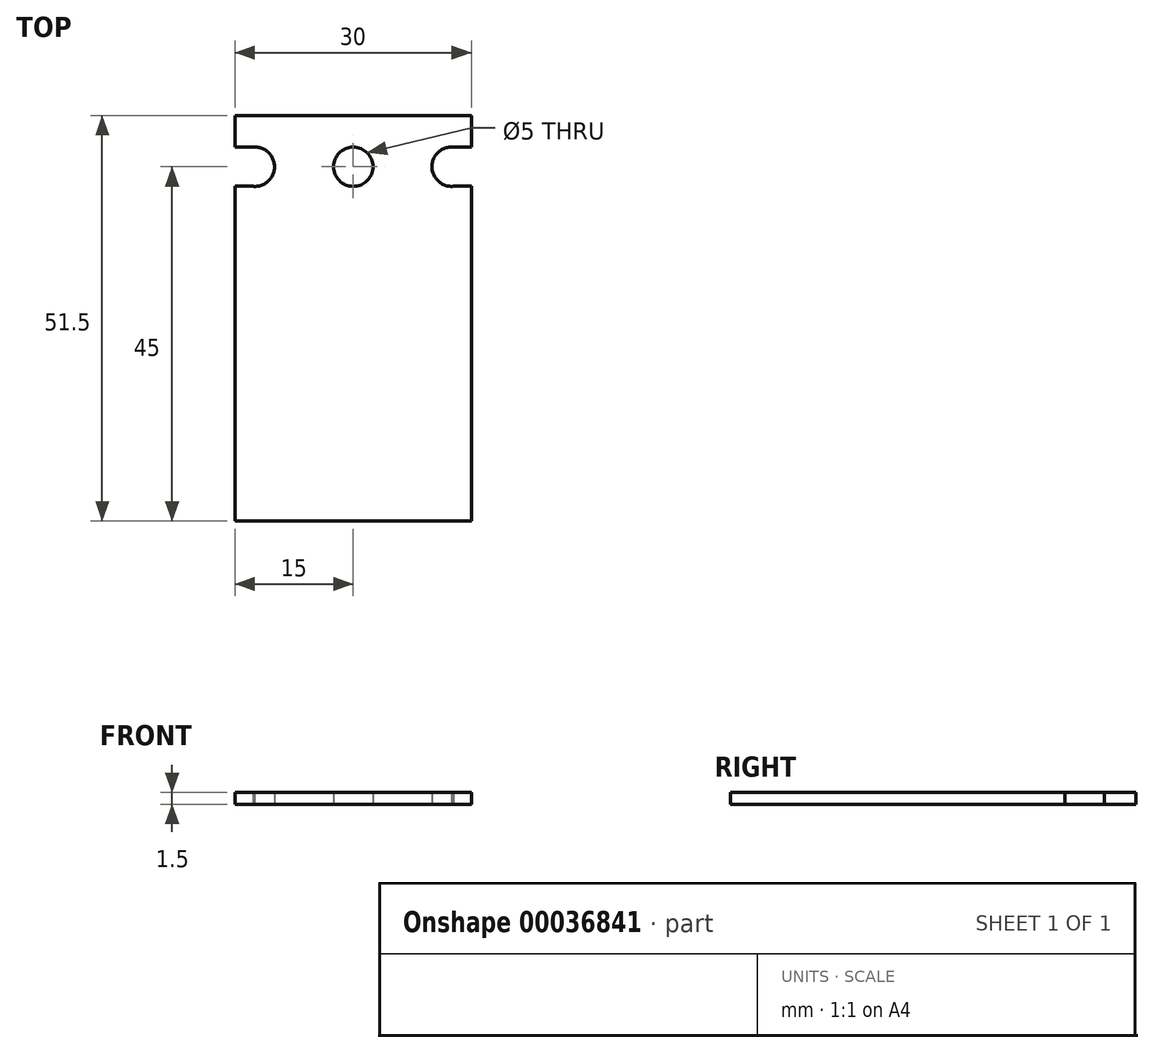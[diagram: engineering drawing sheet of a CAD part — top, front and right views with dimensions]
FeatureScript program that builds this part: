
annotation { "Feature Type Name" : "Feature", "Feature Type Description" : "" }
export const myFeature = defineFeature(function(context is Context, id is Id, definition is map)
    precondition{}
    {
        {
            var Q0;
            Q0=qCreatedBy(makeId("Top.planeOp"),FACE);
            var sketch = newSketch(context, id + "F0", { "sketchPlane" : qUnion([Q0])});
            skLineSegment(sketch, "E0.bottom", {"start": v(-15, 51.5) * mm, "end": v(15, 51.5) * mm});
            skLineSegment(sketch, "E0.top", {"start": v(-15, 0) * mm, "end": v(15, 0) * mm});
            skLineSegment(sketch, "E0.left", {"start": v(-15, 51.5) * mm, "end": v(-15, 0) * mm});
            skLineSegment(sketch, "E0.right", {"start": v(15, 51.5) * mm, "end": v(15, 0) * mm});
            skSolve(sketch);
        }
        {
            var Q0;
            Q0=qCreatedBy(makeId("Top.planeOp"),FACE);
            var sketch = newSketch(context, id + "F1", { "sketchPlane" : qUnion([Q0])});
            skCircle(sketch, "E1", {"center": v(0, 45) * mm, "radius": 2.5 * mm});
            skCircle(sketch, "E2", {"center": v(-12.5, 45) * mm, "radius": 2.5 * mm});
            skCircle(sketch, "E3", {"center": v(12.5, 45) * mm, "radius": 2.5 * mm});
            skLineSegment(sketch, "E4.bottom", {"start": v(12.5, 47.51) * mm, "end": v(15.09, 47.51) * mm});
            skLineSegment(sketch, "E4.top", {"start": v(12.5, 42.51) * mm, "end": v(15.09, 42.51) * mm});
            skLineSegment(sketch, "E4.left", {"start": v(12.5, 47.51) * mm, "end": v(12.5, 42.51) * mm});
            skLineSegment(sketch, "E4.right", {"start": v(15.09, 47.51) * mm, "end": v(15.09, 42.51) * mm});
            skLineSegment(sketch, "E5.bottom", {"start": v(-12.51, 47.51) * mm, "end": v(-15.01, 47.51) * mm});
            skLineSegment(sketch, "E5.top", {"start": v(-12.51, 42.51) * mm, "end": v(-15.01, 42.51) * mm});
            skLineSegment(sketch, "E5.left", {"start": v(-12.51, 47.51) * mm, "end": v(-12.51, 42.51) * mm});
            skLineSegment(sketch, "E5.right", {"start": v(-15.01, 47.51) * mm, "end": v(-15.01, 42.51) * mm});
            skSolve(sketch);
        }
        {
            var Q0;
            Q0=makeQuery(id+"F0.imprint","IMPRINT",FACE,{"disambiguationData":[TD([[makeQuery(id+"F0.imprint","IMPRINT",EDGE,{"derivedFrom":sQuery(id+"F0.wireOp",EDGE,"E0.bottom")}),-1.0]])]});
            extrude(context, id + "F2", {"entities" : qUnion([Q0]), "depth" : 1.5 * mm});
        }
        {
            var Q0;
            Q0 = qSketchRegion(id + "F1", true);
            extrude(context, id + "F3", {"entities" : qUnion([Q0]), "operationType" : NewBodyOperationType.REMOVE, "endBound" : BoundingType.THROUGH_ALL, "depth" : 25.4 * mm});
        }
    });
